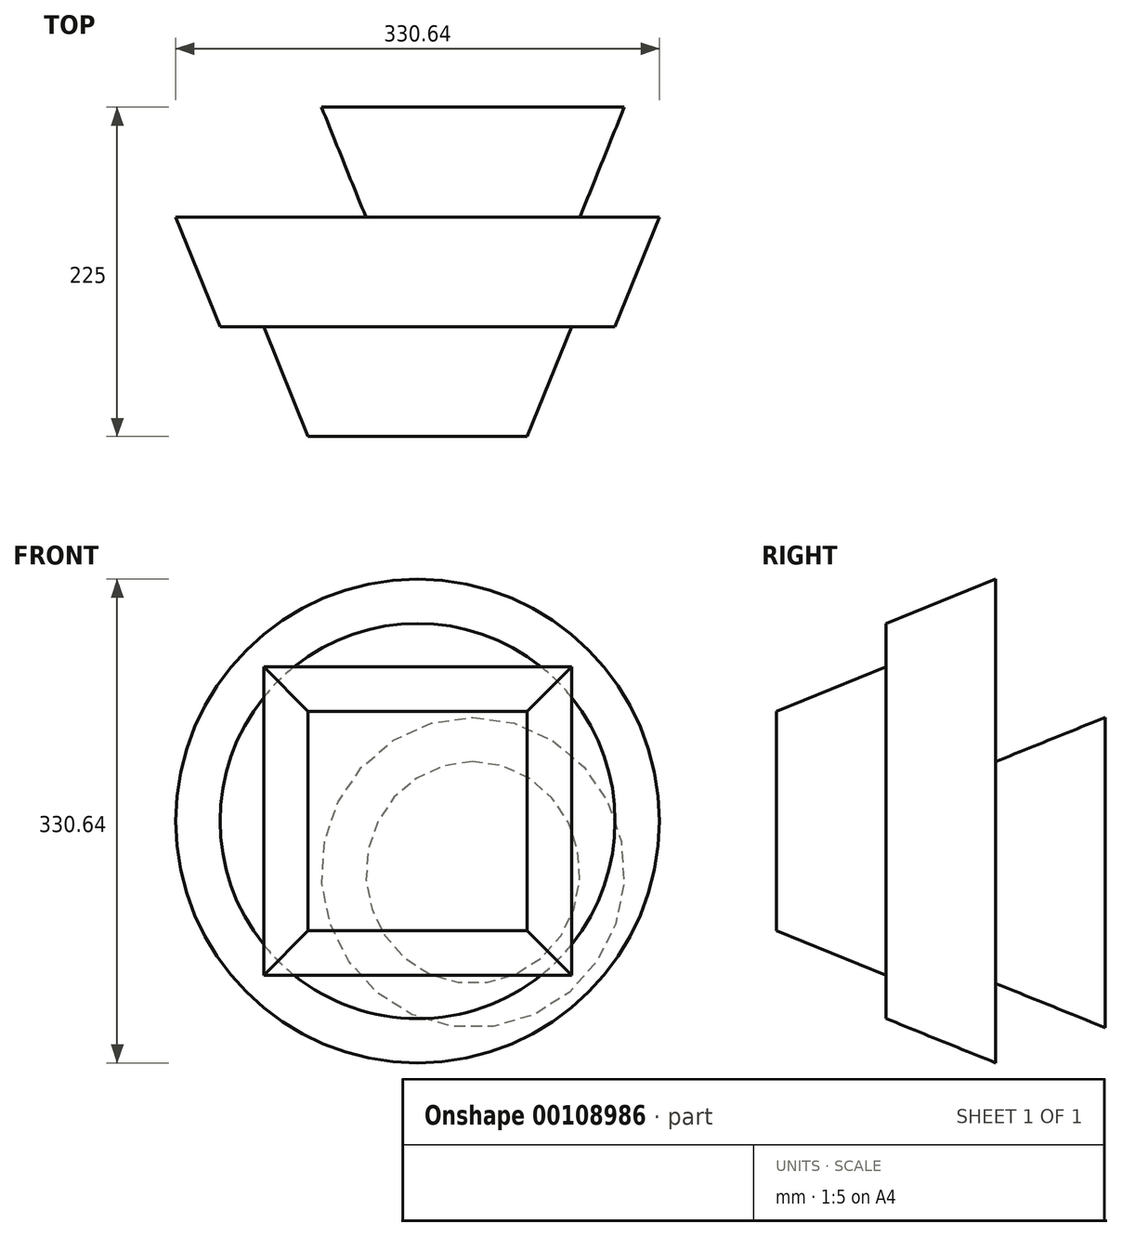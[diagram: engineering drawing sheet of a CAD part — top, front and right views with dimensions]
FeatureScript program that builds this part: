
annotation { "Feature Type Name" : "Feature", "Feature Type Description" : "" }
export const myFeature = defineFeature(function(context is Context, id is Id, definition is map)
    precondition{}
    {
        {
            var Q0;
            Q0=qCreatedBy(makeId("Front.planeOp"),FACE);
            cPlane(context, id + "F0", {"entities" : qUnion([Q0]), "cplaneType" : CPlaneType.OFFSET, "offset" : 75 * mm, "width" : 150 * mm, "height" : 150 * mm});
        }
        {
            var Q0;
            Q0=qCreatedBy(makeId("Front.planeOp"),FACE);
            cPlane(context, id + "F1", {"entities" : qUnion([Q0]), "cplaneType" : CPlaneType.OFFSET, "offset" : 75 * mm, "oppositeDirection" : true, "width" : 150 * mm, "height" : 150 * mm});
        }
        {
            var Q0;
            Q0=qCreatedBy(id+"F0.planeOp",FACE);
            var sketch = newSketch(context, id + "F2", { "sketchPlane" : qUnion([Q0])});
            skLineSegment(sketch, "E0.bottom", {"start": v(75, 75) * mm, "end": v(-75, 75) * mm});
            skLineSegment(sketch, "E0.top", {"start": v(75, -75) * mm, "end": v(-75, -75) * mm});
            skLineSegment(sketch, "E0.left", {"start": v(75, 75) * mm, "end": v(75, -75) * mm});
            skLineSegment(sketch, "E0.right", {"start": v(-75, 75) * mm, "end": v(-75, -75) * mm});
            skPoint(sketch, "E0.middle", {"position": v(0, 0) * mm});
            skSolve(sketch);
        }
        {
            var Q0;
            Q0=qCreatedBy(makeId("Front.planeOp"),FACE);
            var sketch = newSketch(context, id + "F3", { "sketchPlane" : qUnion([Q0])});
            skCircle(sketch, "E1", {"center": v(0, 0) * mm, "radius": 135.02 * mm});
            skSolve(sketch);
        }
        {
            var Q0;
            Q0=qCreatedBy(id+"F1.planeOp",FACE);
            var sketch = newSketch(context, id + "F4", { "sketchPlane" : qUnion([Q0])});
            skEllipse(sketch, "E2", {"center": v(37.8, -35.22) * mm, "majorRadius": 73.19 * mm, "minorRadius": 75.8 * mm, "majorAxis": v(-1, 0)});
            skSolve(sketch);
        }
        {
            var Q0;
            Q0 = qSketchRegion(id + "F2", true);
            var Q1;
            Q1 = qSketchRegion(id + "F3", true);
            var Q2;
            Q2 = qSketchRegion(id + "F4", true);
            var Q3;
            Q3 = qBodyType(qCreatedBy(id + "F4" ,EDGE), BodyType.WIRE);
            var Q4;
            Q4=sQuery(id+"F3.wireOp",EDGE,"E1");
            var Q5;
            Q5 = qBodyType(qCreatedBy(id + "F2" ,EDGE), BodyType.WIRE);
            extrude(context, id + "F5", {"entities" : qUnion([Q0, Q1, Q2]), "surfaceEntities" : qUnion([Q3, Q4, Q5]), "oppositeDirection" : true, "depth" : 75 * mm, "hasDraft" : true, "draftAngle" : 22 * degree});
        }
    });
